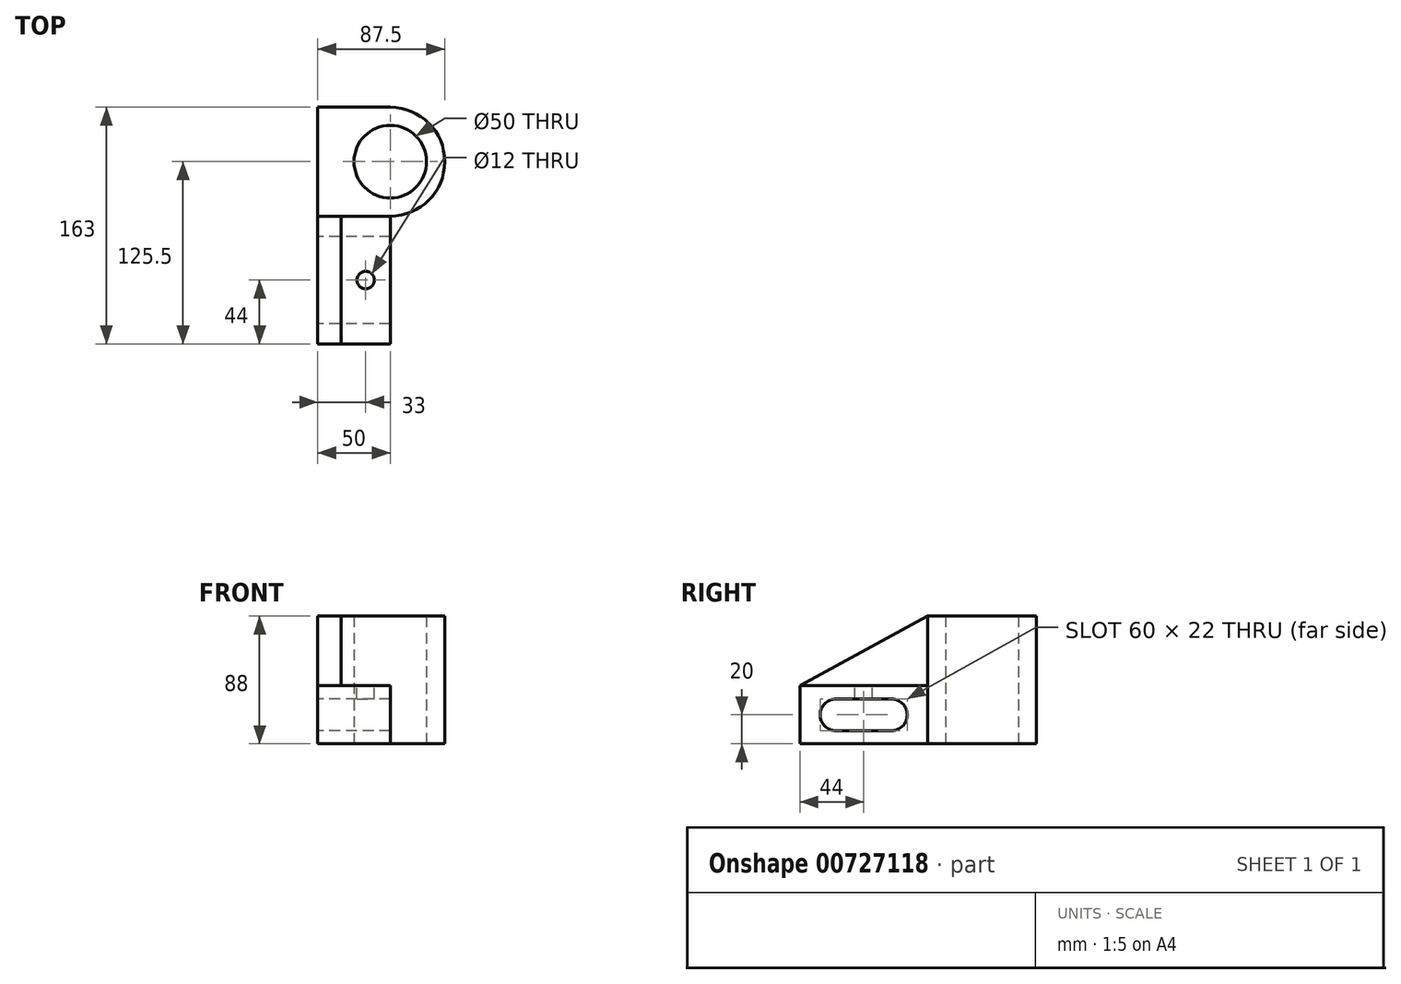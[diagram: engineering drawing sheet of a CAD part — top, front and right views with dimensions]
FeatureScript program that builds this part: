
annotation { "Feature Type Name" : "Feature", "Feature Type Description" : "" }
export const myFeature = defineFeature(function(context is Context, id is Id, definition is map)
    precondition{}
    {
        {
            var Q0;
            Q0=qCreatedBy(makeId("Top.planeOp"),FACE);
            var sketch = newSketch(context, id + "F0", { "sketchPlane" : qUnion([Q0])});
            skLineSegment(sketch, "E0.bottom", {"start": v(0, 0) * mm, "end": v(50, 0) * mm});
            skLineSegment(sketch, "E0.top", {"start": v(0, 75) * mm, "end": v(50, 75) * mm});
            skLineSegment(sketch, "E0.left", {"start": v(0, 0) * mm, "end": v(0, 75) * mm});
            skCircle(sketch, "E1", {"center": v(50, 37.5) * mm, "radius": 25 * mm});
            skArc(sketch, "E2", {"start": v(50, 0) * mm, "mid": v(87.5, 37.5) * mm, "end": v(50, 75) * mm});
            skSolve(sketch);
        }
        {
            var Q0;
            Q0 = qSketchRegion(id + "F0", true);
            extrude(context, id + "F1", {"entities" : qUnion([Q0]), "depth" : 88 * mm, "offsetDistance" : 25 * mm});
        }
        {
            var Q0;
            Q0=qCreatedBy(makeId("Right.planeOp"),FACE);
            var sketch = newSketch(context, id + "F2", { "sketchPlane" : qUnion([Q0])});
            skLineSegment(sketch, "E3.bottom", {"start": v(0, 0) * mm, "end": v(-88, 0) * mm});
            skLineSegment(sketch, "E3.top", {"start": v(0, 40) * mm, "end": v(-88, 40) * mm});
            skLineSegment(sketch, "E3.left", {"start": v(0, 0) * mm, "end": v(0, 40) * mm});
            skLineSegment(sketch, "E3.right", {"start": v(-88, 0) * mm, "end": v(-88, 40) * mm});
            skLineSegment(sketch, "E4", {"start": v(-14, 20) * mm, "end": v(-25, 20) * mm});
            skArc(sketch, "E5", {"start": v(-25, 9) * mm, "mid": v(-14, 20) * mm, "end": v(-25, 31) * mm});
            skLineSegment(sketch, "E6", {"start": v(-25, 20) * mm, "end": v(-63, 20) * mm});
            skArc(sketch, "E7", {"start": v(-63, 31) * mm, "mid": v(-74, 20) * mm, "end": v(-63, 9) * mm});
            skLineSegment(sketch, "E8", {"start": v(-25, 31) * mm, "end": v(-63, 31) * mm});
            skLineSegment(sketch, "E9", {"start": v(-63, 9) * mm, "end": v(-25, 9) * mm});
            skSolve(sketch);
        }
        {
            var Q0;
            Q0 = qSketchRegion(id + "F2", true);
            extrude(context, id + "F3", {"entities" : qUnion([Q0]), "operationType" : NewBodyOperationType.ADD, "depth" : 50 * mm, "offsetDistance" : 25 * mm});
        }
        {
            var Q0;
            Q0=qCreatedBy(makeId("Right.planeOp"),FACE);
            var sketch = newSketch(context, id + "F4", { "sketchPlane" : qUnion([Q0])});
            skLineSegment(sketch, "E10", {"start": v(0, 40) * mm, "end": v(0, 88) * mm});
            skLineSegment(sketch, "E11", {"start": v(0, 40) * mm, "end": v(-88, 40) * mm});
            skLineSegment(sketch, "E12", {"start": v(-88, 40) * mm, "end": v(0, 88) * mm});
            skSolve(sketch);
        }
        {
            var Q0;
            Q0 = qSketchRegion(id + "F4", true);
            extrude(context, id + "F5", {"entities" : qUnion([Q0]), "operationType" : NewBodyOperationType.ADD, "depth" : 16 * mm, "offsetDistance" : 25 * mm});
        }
        {
            var Q0;
            Q0=makeQuery(id+"F3.opExtrude","SWEPT_FACE",FACE,{"disambiguationData":[OSD([sQuery(id+"F2.wireOp",EDGE,"E3.top")])]});
            var sketch = newSketch(context, id + "F6", { "sketchPlane" : qUnion([Q0])});
            skLineSegment(sketch, "E13", {"start": v(33, -38) * mm, "end": v(33, -44) * mm});
            skCircle(sketch, "E14", {"center": v(33, -44) * mm, "radius": 6 * mm});
            skSolve(sketch);
        }
        {
            var Q0;
            Q0 = qSketchRegion(id + "F6", true);
            extrude(context, id + "F7", {"entities" : qUnion([Q0]), "operationType" : NewBodyOperationType.REMOVE, "endBound" : BoundingType.UP_TO_NEXT, "oppositeDirection" : true, "depth" : 25 * mm, "offsetDistance" : 25 * mm});
        }
    });
